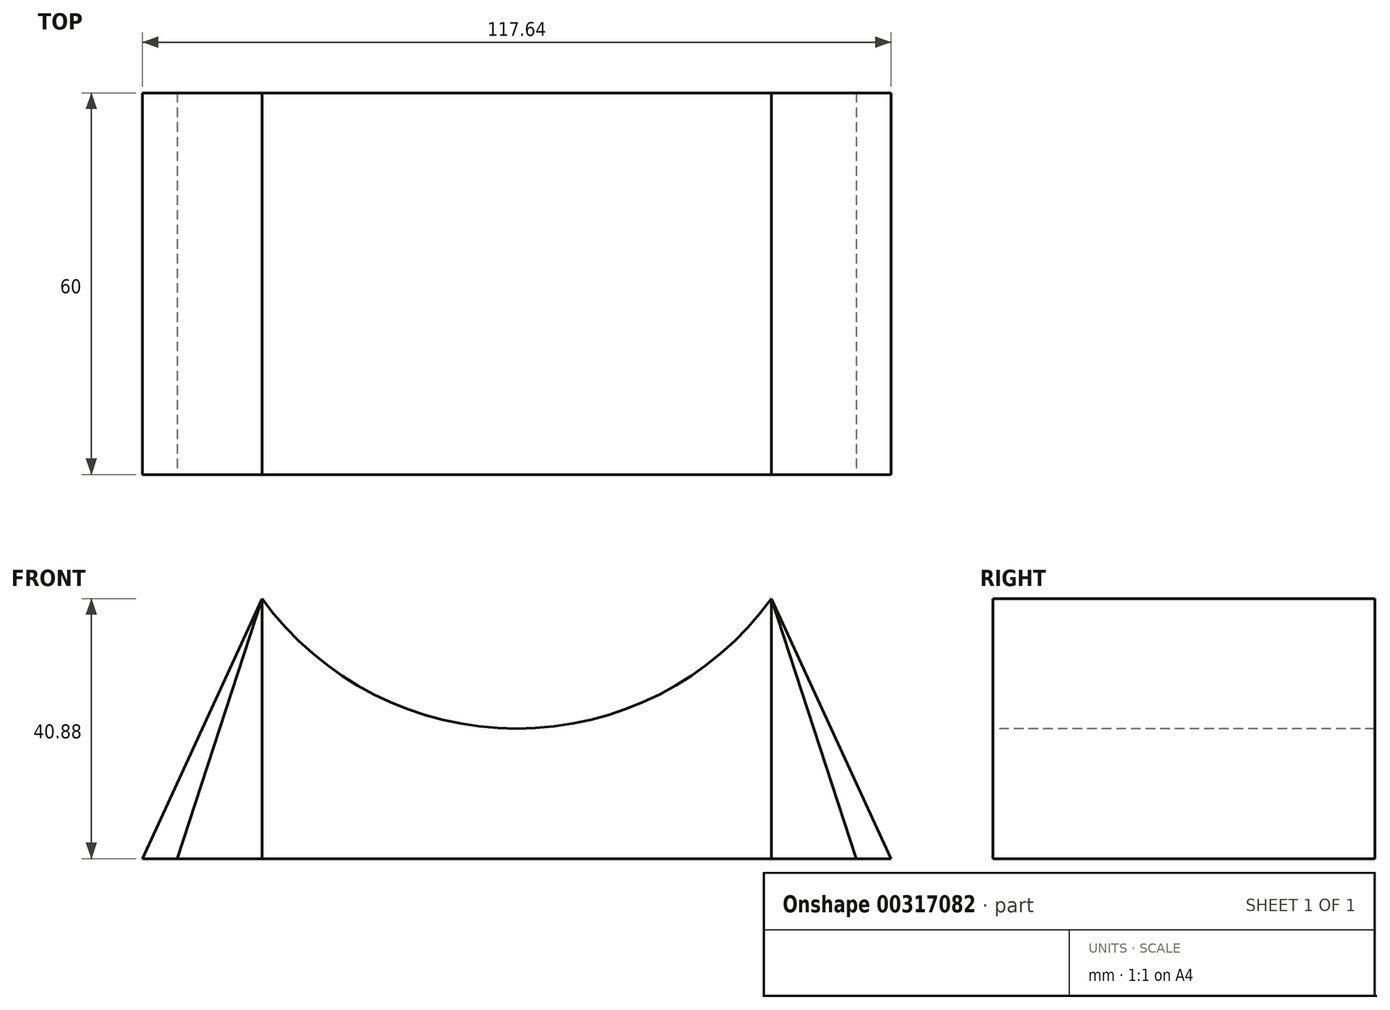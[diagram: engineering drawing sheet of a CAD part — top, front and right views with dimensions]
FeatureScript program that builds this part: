
annotation { "Feature Type Name" : "Feature", "Feature Type Description" : "" }
export const myFeature = defineFeature(function(context is Context, id is Id, definition is map)
    precondition{}
    {
        {
            var Q0;
            Q0=qCreatedBy(makeId("Front.planeOp"),FACE);
            var sketch = newSketch(context, id + "F0", { "sketchPlane" : qUnion([Q0])});
            skLineSegment(sketch, "E0.top", {"start": v(40, -20.44) * mm, "end": v(-40, -20.44) * mm});
            skLineSegment(sketch, "E0.left", {"start": v(40, 20.44) * mm, "end": v(40, -20.44) * mm});
            skLineSegment(sketch, "E0.right", {"start": v(-40, 20.44) * mm, "end": v(-40, -20.44) * mm});
            skPoint(sketch, "E0.middle", {"position": v(0, 0) * mm});
            skArc(sketch, "E1", {"start": v(-40, 20.44) * mm, "mid": v(0, 0) * mm, "end": v(40, 20.44) * mm});
            skLineSegment(sketch, "E2", {"start": v(-40, 20.44) * mm, "end": v(-58.82, -20.44) * mm});
            skLineSegment(sketch, "E3", {"start": v(40, 20.44) * mm, "end": v(58.82, -20.44) * mm});
            skLineSegment(sketch, "E4", {"start": v(-40, 20.44) * mm, "end": v(-53.34, -20.44) * mm});
            skLineSegment(sketch, "E5", {"start": v(-58.82, -20.44) * mm, "end": v(-53.34, -20.44) * mm});
            skLineSegment(sketch, "E6", {"start": v(40, 20.44) * mm, "end": v(53.34, -20.44) * mm});
            skLineSegment(sketch, "E7", {"start": v(53.34, -20.44) * mm, "end": v(58.82, -20.44) * mm});
            skLineSegment(sketch, "E8", {"start": v(-53.34, -20.44) * mm, "end": v(-40, -20.44) * mm});
            skLineSegment(sketch, "E9", {"start": v(40, -20.44) * mm, "end": v(53.34, -20.44) * mm});
            skSolve(sketch);
        }
        {
            var Q0;
            Q0=makeQuery(id+"F0.imprint","IMPRINT",FACE,{"disambiguationData":[TD([[makeQuery(id+"F0.imprint","IMPRINT",EDGE,{"derivedFrom":sQuery(id+"F0.wireOp",EDGE,"E0.top")}),-1.0]])]});
            extrude(context, id + "F1", {"entities" : qUnion([Q0]), "oppositeDirection" : true, "depth" : 60 * mm, "offsetDistance" : 25 * mm});
        }
        {
            var Q0;
            Q0=makeQuery(id+"F0.imprint","IMPRINT",FACE,{"disambiguationData":[TD([[makeQuery(id+"F0.imprint","IMPRINT",EDGE,{"derivedFrom":sQuery(id+"F0.wireOp",EDGE,"E2")}),1.0]])]});
            var Q1;
            Q1=makeQuery(id+"F0.imprint","IMPRINT",FACE,{"disambiguationData":[TD([[makeQuery(id+"F0.imprint","IMPRINT",EDGE,{"derivedFrom":sQuery(id+"F0.wireOp",EDGE,"E3")}),-1.0]])]});
            extrude(context, id + "F2", {"entities" : qUnion([Q0, Q1]), "oppositeDirection" : true, "depth" : 60 * mm, "offsetDistance" : 25 * mm});
        }
        {
            var Q0;
            Q0=makeQuery(id+"F0.imprint","IMPRINT",FACE,{"disambiguationData":[TD([[makeQuery(id+"F0.imprint","IMPRINT",EDGE,{"derivedFrom":sQuery(id+"F0.wireOp",EDGE,"E0.right")}),-1.0]])]});
            var Q1;
            Q1=makeQuery(id+"F0.imprint","IMPRINT",FACE,{"disambiguationData":[TD([[makeQuery(id+"F0.imprint","IMPRINT",EDGE,{"derivedFrom":sQuery(id+"F0.wireOp",EDGE,"E0.left")}),1.0]])]});
            extrude(context, id + "F3", {"entities" : qUnion([Q0, Q1]), "oppositeDirection" : true, "depth" : 60 * mm, "offsetDistance" : 25 * mm});
        }
    });
